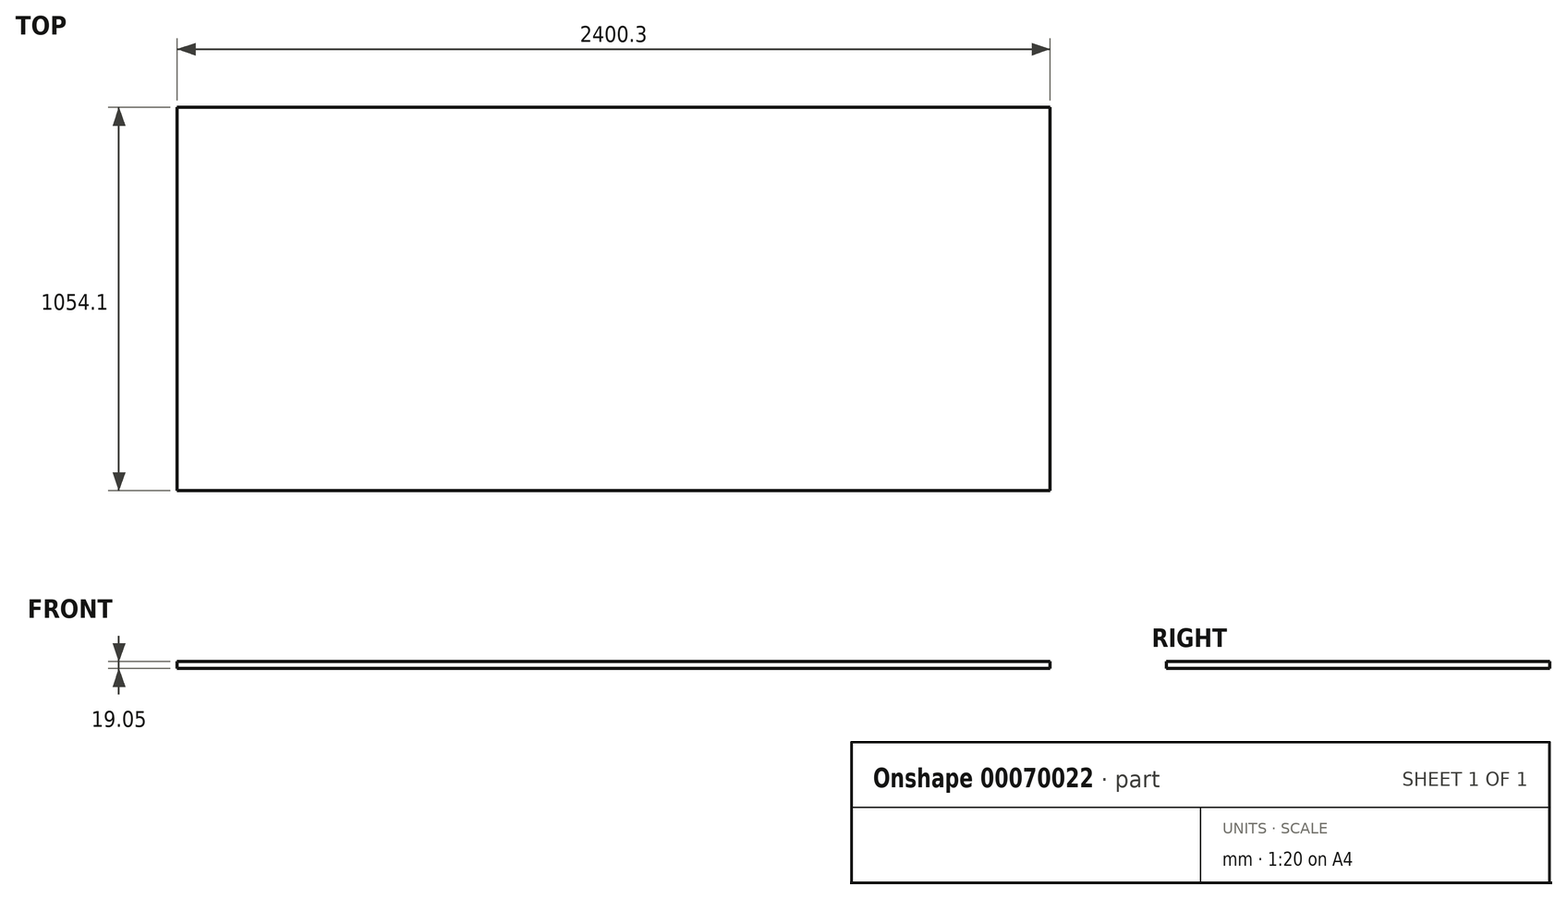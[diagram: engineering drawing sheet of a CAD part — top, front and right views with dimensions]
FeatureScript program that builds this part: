
annotation { "Feature Type Name" : "Feature", "Feature Type Description" : "" }
export const myFeature = defineFeature(function(context is Context, id is Id, definition is map)
    precondition{}
    {
        {
            var Q0;
            Q0=qCreatedBy(makeId("Top.planeOp"),FACE);
            var sketch = newSketch(context, id + "F0", { "sketchPlane" : qUnion([Q0])});
            skLineSegment(sketch, "E0.bottom", {"start": v(0, 0) * mm, "end": v(2400.3, 0) * mm});
            skLineSegment(sketch, "E0.top", {"start": v(0, 1054.1) * mm, "end": v(2400.3, 1054.1) * mm});
            skLineSegment(sketch, "E0.left", {"start": v(0, 0) * mm, "end": v(0, 1054.1) * mm});
            skLineSegment(sketch, "E0.right", {"start": v(2400.3, 0) * mm, "end": v(2400.3, 1054.1) * mm});
            skSolve(sketch);
        }
        {
            var Q0;
            Q0=makeQuery(id+"F0.imprint","IMPRINT",FACE,{"disambiguationData":[TD([[makeQuery(id+"F0.imprint","IMPRINT",EDGE,{"derivedFrom":sQuery(id+"F0.wireOp",EDGE,"E0.bottom")}),1.0]])]});
            extrude(context, id + "F1", {"entities" : qUnion([Q0]), "depth" : 19.05 * mm});
        }
    });
